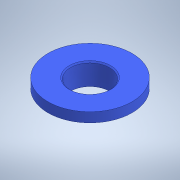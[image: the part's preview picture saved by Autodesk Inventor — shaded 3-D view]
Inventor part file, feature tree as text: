
AUTODESK INVENTOR PART (.ipt)
format: ipt  version: 2022 (Build 260153000, 153)  size: 131,584 bytes
history: native  units: mm
features: extrude x2, sketch x2, chamfer x1, projected_geometry x1
ambient origin geometry x8: Origin, YZ Plane, XZ Plane, XY Plane, X Axis, Y Axis, Z Axis, Center Point
bodies: Solid1 (feature_tree)
feature tree (6):
  extrude  "Extrusion1"  Depth=20.0mm
  extrude  "Extrusion2"  Depth=4.0mm
  chamfer  "Chamfer1"  Distance=4.0mm
  sketch  "Sketch1"  dims[d0=16.3mm d1=20.0mm]
  sketch  "Sketch2"  dims[d2=5.0mm d3=0.0mm d4=35.0mm d5=4.0mm d6=0.0mm d7=0.5mm d8=2.0mm d9=45.0deg]
  projected_geometry  "Projected Loop1"
